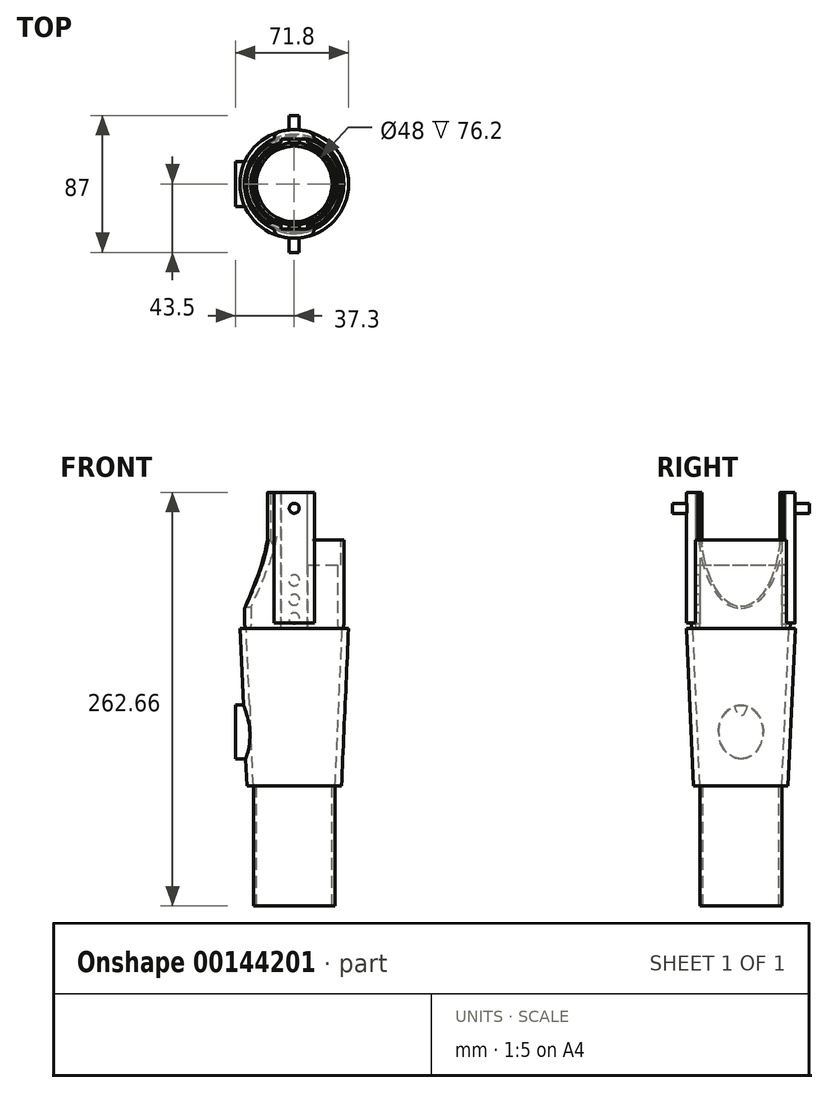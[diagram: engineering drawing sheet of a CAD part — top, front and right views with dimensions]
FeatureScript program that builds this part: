
annotation { "Feature Type Name" : "Feature", "Feature Type Description" : "" }
export const myFeature = defineFeature(function(context is Context, id is Id, definition is map)
    precondition{}
    {
        {
            var Q0;
            Q0=qCreatedBy(makeId("Top.planeOp"),FACE);
            var sketch = newSketch(context, id + "F0", { "sketchPlane" : qUnion([Q0])});
            skCircle(sketch, "E0", {"center": v(0, 0) * mm, "radius": 26 * mm});
            skSolve(sketch);
        }
        {
            var Q0;
            Q0=makeQuery(id+"F0.imprint","IMPRINT",FACE,{"disambiguationData":[TD([[makeQuery(id+"F0.imprint","IMPRINT",EDGE,{"derivedFrom":sQuery(id+"F0.wireOp",EDGE,"E0")}),1.0]])]});
            extrude(context, id + "F1", {"entities" : qUnion([Q0]), "depth" : 76.2 * mm});
        }
        {
            var Q0;
            Q0=makeQuery(id+"F1.opExtrude","CAP_FACE",FACE,{"disambiguationData":[OSD([sQuery(id+"F0.wireOp",EDGE,"E0")])],"isStart":false});
            cPlane(context, id + "F2", {"entities" : qUnion([Q0]), "cplaneType" : CPlaneType.OFFSET, "offset" : 0 * mm, "width" : 150 * mm, "height" : 150 * mm});
        }
        {
            var Q0;
            Q0=qCreatedBy(id+"F2.planeOp",FACE);
            var sketch = newSketch(context, id + "F3", { "sketchPlane" : qUnion([Q0])});
            skCircle(sketch, "E1.0", {"center": v(0, 0) * mm, "radius": 26 * mm});
            skSolve(sketch);
        }
        {
            var Q0;
            Q0=qCreatedBy(id+"F2.planeOp",FACE);
            cPlane(context, id + "F4", {"entities" : qUnion([Q0]), "cplaneType" : CPlaneType.OFFSET, "offset" : 100 * mm, "width" : 150 * mm, "height" : 150 * mm});
        }
        {
            var Q0;
            Q0=qCreatedBy(id+"F4.planeOp",FACE);
            var sketch = newSketch(context, id + "F5", { "sketchPlane" : qUnion([Q0])});
            skCircle(sketch, "E2", {"center": v(0, 0) * mm, "radius": 30.5 * mm});
            skSolve(sketch);
        }
        {
            var Q1;
            Q1=makeQuery(id+"F3.imprint","IMPRINT",FACE,{"disambiguationData":[TD([[makeQuery(id+"F3.imprint","IMPRINT",EDGE,{"derivedFrom":sQuery(id+"F3.wireOp",EDGE,"E1.0")}),1.0]])]});
            var Q2;
            Q2=makeQuery(id+"F5.imprint","IMPRINT",FACE,{"disambiguationData":[TD([[makeQuery(id+"F5.imprint","IMPRINT",EDGE,{"derivedFrom":sQuery(id+"F5.wireOp",EDGE,"E2")}),1.0]])]});
            loft(context, id + "F6", {"operationType" : NewBodyOperationType.ADD, "sheetProfilesArray" : [{ "sheetProfileEntities" : qUnion([Q1]) }, { "sheetProfileEntities" : qUnion([Q2]) }]});
        }
        {
            var Q0;
            Q0=qCreatedBy(id+"F2.planeOp",FACE);
            var sketch = newSketch(context, id + "F7", { "sketchPlane" : qUnion([Q0])});
            skCircle(sketch, "E3", {"center": v(0, 0) * mm, "radius": 24 * mm});
            skSolve(sketch);
        }
        {
            var Q0;
            Q0=qCreatedBy(id+"F4.planeOp",FACE);
            var sketch = newSketch(context, id + "F8", { "sketchPlane" : qUnion([Q0])});
            skCircle(sketch, "E4", {"center": v(0, 0) * mm, "radius": 28.5 * mm});
            skSolve(sketch);
        }
        {
            var Q1;
            Q1=makeQuery(id+"F8.imprint","IMPRINT",FACE,{"disambiguationData":[TD([[makeQuery(id+"F8.imprint","IMPRINT",EDGE,{"derivedFrom":sQuery(id+"F8.wireOp",EDGE,"E4")}),1.0]])]});
            var Q2;
            Q2=qSketchRegion(id+"F7",true);
            loft(context, id + "F9", {"operationType" : NewBodyOperationType.REMOVE, "sheetProfilesArray" : [{ "sheetProfileEntities" : qUnion([Q1]) }, { "sheetProfileEntities" : qUnion([Q2]) }]});
        }
        {
            var Q0;
            Q0=qCreatedBy(makeId("Top.planeOp"),FACE);
            var sketch = newSketch(context, id + "F10", { "sketchPlane" : qUnion([Q0])});
            skCircle(sketch, "E5", {"center": v(0, 0) * mm, "radius": 24 * mm});
            skSolve(sketch);
        }
        {
            var Q1;
            Q1=qSketchRegion(id+"F7",true);
            var Q2;
            Q2=qSketchRegion(id+"F10",true);
            loft(context, id + "F11", {"operationType" : NewBodyOperationType.REMOVE, "sheetProfilesArray" : [{ "sheetProfileEntities" : qUnion([Q1]) }, { "sheetProfileEntities" : qUnion([Q2]) }]});
        }
        {
            var Q0;
            Q0=qCreatedBy(id+"F4.planeOp",FACE);
            var sketch = newSketch(context, id + "F12", { "sketchPlane" : qUnion([Q0])});
            skCircle(sketch, "E6", {"center": v(0, 0) * mm, "radius": 31.5 * mm});
            skCircle(sketch, "E7.0", {"center": v(0, 0) * mm, "radius": 27.5 * mm});
            skSolve(sketch);
        }
        {
            var Q0;
            Q0=qSketchRegion(id+"F12",true);
            extrude(context, id + "F13", {"entities" : qUnion([Q0]), "operationType" : NewBodyOperationType.ADD, "depth" : 56.46 * mm});
        }
        {
            var Q0;
            Q0=makeQuery(id+"F13.opExtrude","CAP_EDGE",EDGE,{"disambiguationData":[OSD([sQuery(id+"F12.wireOp",EDGE,"E6")])],"isStart":true});
            fillet(context, id + "F14", {"entities" : qUnion([Q0]), "radius" : 5 * mm, "tangentPropagation" : true, "allowEdgeOverflow" : false});
        }
        {
            var Q0;
            Q0=makeQuery(id+"F13.opExtrude","CAP_FACE",FACE,{"disambiguationData":[OSD([sQuery(id+"F12.wireOp",EDGE,"E6"),sQuery(id+"F12.wireOp",EDGE,"E7.0")])],"isStart":false});
            cPlane(context, id + "F15", {"entities" : qUnion([Q0]), "cplaneType" : CPlaneType.OFFSET, "offset" : 0 * mm, "width" : 150 * mm, "height" : 150 * mm});
        }
        {
            var Q0;
            Q0=qCreatedBy(id+"F15.planeOp",FACE);
            var sketch = newSketch(context, id + "F16", { "sketchPlane" : qUnion([Q0])});
            skCircle(sketch, "E8.0", {"center": v(0, 0) * mm, "radius": 31.5 * mm, "construction": true});
            skCircle(sketch, "E9.0", {"center": v(0, 0) * mm, "radius": 27.5 * mm, "construction": true});
            skArc(sketch, "E10", {"start": v(8.5, -28.5) * mm, "mid": v(29.74, 0) * mm, "end": v(8.5, 28.5) * mm});
            skArc(sketch, "E11", {"start": v(8.5, -24.3) * mm, "mid": v(25.75, 0) * mm, "end": v(8.5, 24.3) * mm});
            skLineSegment(sketch, "E12", {"start": v(8.5, 28.5) * mm, "end": v(8.5, 24.3) * mm});
            skLineSegment(sketch, "E13.MirrorCS", {"start": v(8.5, -28.5) * mm, "end": v(8.5, -24.3) * mm});
            skPoint(sketch, "E14.orphan", {"position": v(0, 29.74) * mm});
            skPoint(sketch, "E15.orphan", {"position": v(0, -25.75) * mm});
            skSolve(sketch);
        }
        {
            var Q0;
            Q0=qSketchRegion(id+"F16",true);
            extrude(context, id + "F17", {"entities" : qUnion([Q0]), "operationType" : NewBodyOperationType.REMOVE, "oppositeDirection" : true, "depth" : 16 * mm});
        }
        {
            var Q0;
            Q0=qCreatedBy(id+"F15.planeOp",FACE);
            var sketch = newSketch(context, id + "F18", { "sketchPlane" : qUnion([Q0])});
            skLineSegment(sketch, "E16.bottom", {"start": v(-8.5, 28.5) * mm, "end": v(8.5, 28.5) * mm});
            skLineSegment(sketch, "E16.top", {"start": v(-8.5, 24) * mm, "end": v(8.5, 24) * mm});
            skLineSegment(sketch, "E16.left", {"start": v(-8.5, 28.5) * mm, "end": v(-8.5, 24) * mm});
            skLineSegment(sketch, "E16.right", {"start": v(8.5, 28.5) * mm, "end": v(8.5, 24) * mm});
            skLineSegment(sketch, "E17", {"start": v(0, 28.5) * mm, "end": v(0, 24) * mm, "construction": true});
            skLineSegment(sketch, "E18.0", {"start": v(8.5, -28.5) * mm, "end": v(8.5, -28.5) * mm});
            skLineSegment(sketch, "E19.MirrorCS", {"start": v(-8.5, -24) * mm, "end": v(8.5, -24) * mm});
            skLineSegment(sketch, "E20.MirrorCS", {"start": v(8.5, -28.5) * mm, "end": v(8.5, -24) * mm});
            skLineSegment(sketch, "E21.MirrorCS", {"start": v(-8.5, -28.5) * mm, "end": v(8.5, -28.5) * mm});
            skLineSegment(sketch, "E22.MirrorCS", {"start": v(-8.5, -28.5) * mm, "end": v(-8.5, -24) * mm});
            skSolve(sketch);
        }
        {
            var Q0;
            Q0=qSketchRegion(id+"F18",true);
            extrude(context, id + "F19", {"entities" : qUnion([Q0]), "operationType" : NewBodyOperationType.REMOVE, "oppositeDirection" : true, "depth" : 56.46 * mm});
        }
        {
            var Q0;
            {var subQ0=sQuery(id+"F12.wireOp",EDGE,"E7.0");Q0=makeQuery(id+"F19.boolean.opBoolean","SPLIT",EDGE,{"disambiguationData":[TD([makeQuery(id+"F19.opExtrude","SWEPT_FACE",FACE,{"disambiguationData":[OSD([sQuery(id+"F18.wireOp",EDGE,"E16.left")])]})])],"derivedFrom":makeQuery(id+"F13.opExtrude","CAP_EDGE",EDGE,{"disambiguationData":[OSD([subQ0])],"isStart":true})});}
            var Q1;
            {var subQ0=sQuery(id+"F12.wireOp",EDGE,"E7.0");Q1=makeQuery(id+"F19.boolean.opBoolean","SPLIT",EDGE,{"disambiguationData":[TD([makeQuery(id+"F19.opExtrude","SWEPT_FACE",FACE,{"disambiguationData":[OSD([sQuery(id+"F18.wireOp",EDGE,"E16.right")])]})])],"derivedFrom":makeQuery(id+"F13.opExtrude","CAP_EDGE",EDGE,{"disambiguationData":[OSD([subQ0])],"isStart":true})});}
            fillet(context, id + "F20", {"entities" : qUnion([Q0, Q1]), "radius" : 5 * mm, "tangentPropagation" : true, "allowEdgeOverflow" : false});
        }
        {
            var Q0;
            Q0=makeQuery(id+"F19.boolean.opBoolean","COPY",FACE,{"derivedFrom":makeQuery(id+"F19.opExtrude","SWEPT_FACE",FACE,{"disambiguationData":[OSD([sQuery(id+"F18.wireOp",EDGE,"E16.bottom")])]})});
            cPlane(context, id + "F21", {"entities" : qUnion([Q0]), "cplaneType" : CPlaneType.OFFSET, "offset" : 0 * mm, "width" : 150 * mm, "height" : 150 * mm});
        }
        {
            var Q0;
            Q0=qCreatedBy(id+"F21.planeOp",FACE);
            var sketch = newSketch(context, id + "F22", { "sketchPlane" : qUnion([Q0])});
            skLineSegment(sketch, "E23.0.0", {"start": v(8.5, 232.66) * mm, "end": v(-8.5, 232.66) * mm, "construction": true});
            skLineSegment(sketch, "E23.0.1", {"start": v(-8.5, 232.66) * mm, "end": v(-8.5, 176.2) * mm, "construction": true});
            skLineSegment(sketch, "E23.0.2", {"start": v(-8.5, 176.2) * mm, "end": v(0, 176.2) * mm, "construction": true});
            skLineSegment(sketch, "E23.0.3", {"start": v(0, 176.2) * mm, "end": v(8.5, 176.2) * mm, "construction": true});
            skLineSegment(sketch, "E23.0.4", {"start": v(8.5, 176.2) * mm, "end": v(8.5, 232.66) * mm, "construction": true});
            skLineSegment(sketch, "E24", {"start": v(0, 232.66) * mm, "end": v(0, 176.2) * mm, "construction": true});
            skCircle(sketch, "E25", {"center": v(0, 206.85) * mm, "radius": 3.45 * mm});
            skCircle(sketch, "E26", {"center": v(0, 194.54) * mm, "radius": 3.45 * mm});
            skCircle(sketch, "E27", {"center": v(0, 182.7) * mm, "radius": 3.45 * mm});
            skSolve(sketch);
        }
        {
            var Q0;
            Q0=qSketchRegion(id+"F22",true);
            extrude(context, id + "F23", {"entities" : qUnion([Q0]), "depth" : 2.5 * mm});
        }
        {
            var Q0;
            Q0=makeQuery(id+"F23.opExtrude","SWEPT_BODY",BODY,{"disambiguationData":[OSD([sQuery(id+"F22.wireOp",EDGE,"E25")])]});
            var Q1;
            Q1=makeQuery(id+"F23.opExtrude","SWEPT_BODY",BODY,{"disambiguationData":[OSD([sQuery(id+"F22.wireOp",EDGE,"E26")])]});
            var Q2;
            Q2=makeQuery(id+"F23.opExtrude","SWEPT_BODY",BODY,{"disambiguationData":[OSD([sQuery(id+"F22.wireOp",EDGE,"E27")])]});
            var Q3;
            Q3=qCreatedBy(makeId("Front.planeOp"),FACE);
            mirror(context, id + "F24", {"operationType" : NewBodyOperationType.ADD, "entities" : qUnion([Q0, Q1, Q2]), "mirrorPlane" : qUnion([Q3])});
        }
        {
            var Q0;
            Q0=qCreatedBy(id+"F15.planeOp",FACE);
            var sketch = newSketch(context, id + "F25", { "sketchPlane" : qUnion([Q0])});
            skCircle(sketch, "E28", {"center": v(0, 0) * mm, "radius": 34.44 * mm});
            skCircle(sketch, "E29.0", {"center": v(0, 0) * mm, "radius": 31.5 * mm});
            skLineSegment(sketch, "E30", {"start": v(12.77, 31.98) * mm, "end": v(12.77, 28.8) * mm});
            skLineSegment(sketch, "E31.MirrorCS", {"start": v(-12.77, 31.98) * mm, "end": v(-12.77, 28.8) * mm});
            skLineSegment(sketch, "E32.MirrorCS", {"start": v(12.77, -31.98) * mm, "end": v(12.77, -28.8) * mm});
            skLineSegment(sketch, "E33.MirrorCS", {"start": v(-12.77, -31.98) * mm, "end": v(-12.77, -28.8) * mm});
            skSolve(sketch);
        }
        {
            var Q0;
            {var subQ1=sQuery(id+"F25.wireOp",EDGE,"E30");Q0=makeQuery(id+"F25.imprint","IMPRINT",FACE,{"disambiguationData":[TD([[makeQuery(id+"F25.imprint","IMPRINT",EDGE,{"derivedFrom":subQ1}),-1.0]])]});}
            var Q1;
            {var subQ1=sQuery(id+"F25.wireOp",EDGE,"E32.MirrorCS");Q1=makeQuery(id+"F25.imprint","IMPRINT",FACE,{"disambiguationData":[TD([[makeQuery(id+"F25.imprint","IMPRINT",EDGE,{"derivedFrom":subQ1}),1.0]])]});}
            extrude(context, id + "F26", {"entities" : qUnion([Q0, Q1]), "operationType" : NewBodyOperationType.ADD, "depth" : 30 * mm, "hasSecondDirection" : true, "secondDirectionOppositeDirection" : true, "secondDirectionDepth" : 53 * mm});
        }
        {
            var Q0;
            Q0=makeQuery(id+"F13.opExtrude","CAP_FACE",FACE,{"disambiguationData":[OSD([sQuery(id+"F12.wireOp",EDGE,"E6"),sQuery(id+"F12.wireOp",EDGE,"E7.0")])],"isStart":false});
            var sketch = newSketch(context, id + "F27", { "sketchPlane" : qUnion([Q0])});
            skLineSegment(sketch, "E34", {"start": v(12.77, 28.8) * mm, "end": v(12.77, 26.86) * mm});
            skLineSegment(sketch, "E35", {"start": v(-12.77, 28.8) * mm, "end": v(-12.77, 24.35) * mm});
            skLineSegment(sketch, "E36.MirrorCS", {"start": v(12.77, -28.8) * mm, "end": v(12.77, -26.86) * mm});
            skLineSegment(sketch, "E37.MirrorCS", {"start": v(-12.77, -28.8) * mm, "end": v(-12.77, -24.35) * mm});
            skSolve(sketch);
        }
        {
            var Q0;
            {var subQ5=sQuery(id+"F27.wireOp",EDGE,"E34");Q0=makeQuery(id+"F27.imprint","IMPRINT",FACE,{"disambiguationData":[TD([[makeQuery(id+"F27.imprint","IMPRINT",EDGE,{"derivedFrom":subQ5}),-1.0]])]});}
            var Q1;
            {var subQ9=sQuery(id+"F27.wireOp",EDGE,"E36.MirrorCS");Q1=makeQuery(id+"F27.imprint","IMPRINT",FACE,{"disambiguationData":[TD([[makeQuery(id+"F27.imprint","IMPRINT",EDGE,{"derivedFrom":subQ9}),1.0]])]});}
            extrude(context, id + "F28", {"entities" : qUnion([Q0, Q1]), "operationType" : NewBodyOperationType.ADD, "depth" : 30 * mm, "hasSecondDirection" : true, "secondDirectionOppositeDirection" : true, "secondDirectionDepth" : 25 * mm});
        }
        {
            var Q0;
            Q0=makeQuery(id+"F26.opExtrude","SWEPT_EDGE",EDGE,{"disambiguationData":[OSD([sQuery(id+"F25.wireOp",EDGE,"E28"),sQuery(id+"F25.wireOp",EDGE,"E31.MirrorCS")])]});
            var Q1;
            Q1=makeQuery(id+"F26.opExtrude","SWEPT_EDGE",EDGE,{"disambiguationData":[OSD([sQuery(id+"F25.wireOp",EDGE,"E28"),sQuery(id+"F25.wireOp",EDGE,"E33.MirrorCS")])]});
            var Q2;
            Q2=makeQuery(id+"F26.opExtrude","SWEPT_EDGE",EDGE,{"disambiguationData":[OSD([sQuery(id+"F25.wireOp",EDGE,"E28"),sQuery(id+"F25.wireOp",EDGE,"E32.MirrorCS")])]});
            var Q3;
            Q3=makeQuery(id+"F26.opExtrude","SWEPT_EDGE",EDGE,{"disambiguationData":[OSD([sQuery(id+"F25.wireOp",EDGE,"E28"),sQuery(id+"F25.wireOp",EDGE,"E30")])]});
            fillet(context, id + "F29", {"entities" : qUnion([Q0, Q1, Q2, Q3]), "radius" : 5 * mm, "tangentPropagation" : true, "allowEdgeOverflow" : false});
        }
        {
            var Q0;
            Q0=makeQuery(id+"F28.opExtrude","SWEPT_EDGE",EDGE,{"disambiguationData":[OSD([sQuery(id+"F12.wireOp",EDGE,"E7.0"),sQuery(id+"F27.wireOp",EDGE,"E37.MirrorCS")])]});
            fillet(context, id + "F30", {"entities" : qUnion([Q0]), "radius" : 1 * mm, "tangentPropagation" : true, "allowEdgeOverflow" : false});
        }
        {
            var Q0;
            Q0=makeQuery(id+"F28.opExtrude","SWEPT_EDGE",EDGE,{"disambiguationData":[OSD([sQuery(id+"F12.wireOp",EDGE,"E7.0"),sQuery(id+"F27.wireOp",EDGE,"E35")])]});
            fillet(context, id + "F31", {"entities" : qUnion([Q0]), "radius" : 1 * mm, "tangentPropagation" : true, "allowEdgeOverflow" : false});
        }
        {
            var Q0;
            Q0=makeQuery(id+"F28.opExtrude","SWEPT_EDGE",EDGE,{"disambiguationData":[OSD([sQuery(id+"F16.wireOp",EDGE,"E10"),sQuery(id+"F27.wireOp",EDGE,"E36.MirrorCS")])]});
            fillet(context, id + "F32", {"entities" : qUnion([Q0]), "radius" : 1 * mm, "tangentPropagation" : true, "allowEdgeOverflow" : false});
        }
        {
            var Q0;
            Q0=makeQuery(id+"F28.opExtrude","SWEPT_EDGE",EDGE,{"disambiguationData":[OSD([sQuery(id+"F16.wireOp",EDGE,"E10"),sQuery(id+"F27.wireOp",EDGE,"E34")])]});
            fillet(context, id + "F33", {"entities" : qUnion([Q0]), "radius" : 1 * mm, "tangentPropagation" : true, "allowEdgeOverflow" : false});
        }
        {
            var Q0;
            {var subQ0=sQuery(id+"F18.wireOp",EDGE,"E16.bottom");Q0=makeQuery(id+"F28.boolean.opBoolean","MERGE",FACE,{"derivedFrom":[makeQuery(id+"F19.boolean.opBoolean","COPY",FACE,{"derivedFrom":makeQuery(id+"F19.opExtrude","SWEPT_FACE",FACE,{"disambiguationData":[OSD([subQ0])]})}),makeQuery(id+"F28.opExtrude","SWEPT_FACE",FACE,{"disambiguationData":[OSD([subQ0])]})]});}
            var sketch = newSketch(context, id + "F34", { "sketchPlane" : qUnion([Q0])});
            skLineSegment(sketch, "E38.0", {"start": v(-8.5, 262.66) * mm, "end": v(8.5, 262.66) * mm, "construction": true});
            skLineSegment(sketch, "E39", {"start": v(0, 262.66) * mm, "end": v(0, 242.66) * mm, "construction": true});
            skPoint(sketch, "E39.endSnap0", {"position": v(0, 262.66) * mm});
            skCircle(sketch, "E40", {"center": v(0, 252.66) * mm, "radius": 3.18 * mm});
            skSolve(sketch);
        }
        {
            var Q0;
            Q0=makeQuery(id+"F34.imprint","IMPRINT",FACE,{"disambiguationData":[TD([[makeQuery(id+"F34.imprint","IMPRINT",EDGE,{"derivedFrom":sQuery(id+"F34.wireOp",EDGE,"E40")}),1.0]])]});
            extrude(context, id + "F35", {"entities" : qUnion([Q0]), "oppositeDirection" : true, "depth" : 15 * mm});
        }
        {
            var Q0;
            Q0=makeQuery(id+"F35.opExtrude","SWEPT_BODY",BODY,{"disambiguationData":[OSD([sQuery(id+"F34.wireOp",EDGE,"E40")])]});
            var Q1;
            Q1=qCreatedBy(makeId("Front.planeOp"),FACE);
            mirror(context, id + "F36", {"operationType" : NewBodyOperationType.ADD, "entities" : qUnion([Q0]), "mirrorPlane" : qUnion([Q1])});
        }
        {
            var Q0;
            Q0=qCreatedBy(makeId("Right.planeOp"),FACE);
            cPlane(context, id + "F37", {"entities" : qUnion([Q0]), "cplaneType" : CPlaneType.OFFSET, "offset" : 55 * mm, "oppositeDirection" : true, "width" : 150 * mm, "height" : 150 * mm});
        }
        {
            var Q0;
            Q0=qCreatedBy(id+"F37.planeOp",FACE);
            var sketch = newSketch(context, id + "F38", { "sketchPlane" : qUnion([Q0])});
            skLineSegment(sketch, "E41", {"start": v(-31.5, 188.04) * mm, "end": v(-31.5, 188.5) * mm, "construction": true});
            skLineSegment(sketch, "E42", {"start": v(31.5, 188.5) * mm, "end": v(31.5, 188.04) * mm, "construction": true});
            skEllipse(sketch, "E43", {"center": v(0, 241.57) * mm, "majorRadius": 25.3 * mm, "minorRadius": 51.5 * mm, "majorAxis": v(-1, 0)});
            skSolve(sketch);
        }
        {
            var Q0;
            Q0=qSketchRegion(id+"F38",true);
            extrude(context, id + "F39", {"entities" : qUnion([Q0]), "operationType" : NewBodyOperationType.REMOVE, "depth" : 40 * mm});
        }
        {
            var Q0;
            Q0=makeQuery(id+"F39.boolean.opBoolean","INTERSECT",EDGE,{"derivedFrom":[makeQuery(id+"F13.opExtrude","SWEPT_FACE",FACE,{"disambiguationData":[OSD([sQuery(id+"F12.wireOp",EDGE,"E6")])]}),makeQuery(id+"F39.opExtrude","SWEPT_FACE",FACE,{"disambiguationData":[OSD([sQuery(id+"F38.wireOp",EDGE,"E43")])]})]});
            fillet(context, id + "F40", {"entities" : qUnion([Q0]), "radius" : 1 * mm, "tangentPropagation" : true, "allowEdgeOverflow" : false});
        }
        {
            var Q0;
            {var subQ0=sQuery(id+"F12.wireOp",EDGE,"E6");var subQ1=sQuery(id+"F12.wireOp",EDGE,"E7.0");var subQ6=sQuery(id+"F25.wireOp",EDGE,"E33.MirrorCS");var subQ7=makeQuery(id+"F26.opExtrude","SWEPT_FACE",FACE,{"disambiguationData":[OSD([subQ6])]});Q0=makeQuery(id+"F39.boolean.opBoolean","SPLIT",FACE,{"disambiguationData":[TD([subQ7])],"derivedFrom":makeQuery(id+"F28.boolean.opBoolean","SPLIT",FACE,{"disambiguationData":[TD([makeQuery(id+"F13.opExtrude","SWEPT_FACE",FACE,{"disambiguationData":[OSD([subQ1])]})])],"derivedFrom":makeQuery(id+"F13.opExtrude","CAP_FACE",FACE,{"disambiguationData":[OSD([subQ0,subQ1])],"isStart":false})})});}
            var Q1;
            {var subQ0=sQuery(id+"F12.wireOp",EDGE,"E6");var subQ1=sQuery(id+"F12.wireOp",EDGE,"E7.0");var subQ6=sQuery(id+"F25.wireOp",EDGE,"E31.MirrorCS");var subQ7=makeQuery(id+"F26.opExtrude","SWEPT_FACE",FACE,{"disambiguationData":[OSD([subQ6])]});Q1=makeQuery(id+"F39.boolean.opBoolean","SPLIT",FACE,{"disambiguationData":[TD([subQ7])],"derivedFrom":makeQuery(id+"F28.boolean.opBoolean","SPLIT",FACE,{"disambiguationData":[TD([makeQuery(id+"F13.opExtrude","SWEPT_FACE",FACE,{"disambiguationData":[OSD([subQ1])]})])],"derivedFrom":makeQuery(id+"F13.opExtrude","CAP_FACE",FACE,{"disambiguationData":[OSD([subQ0,subQ1])],"isStart":false})})});}
            var Q2;
            Q2=makeQuery(id+"F28.boolean.opBoolean","MERGE",FACE,{"derivedFrom":[makeQuery(id+"F26.opExtrude","CAP_FACE",FACE,{"disambiguationData":[OSD([sQuery(id+"F25.wireOp",EDGE,"E28"),sQuery(id+"F25.wireOp",EDGE,"E29.0"),sQuery(id+"F25.wireOp",EDGE,"E32.MirrorCS"),sQuery(id+"F25.wireOp",EDGE,"E33.MirrorCS")])],"isStart":false}),makeQuery(id+"F28.opExtrude","CAP_FACE",FACE,{"disambiguationData":[OSD([sQuery(id+"F12.wireOp",EDGE,"E6"),sQuery(id+"F12.wireOp",EDGE,"E7.0"),sQuery(id+"F16.wireOp",EDGE,"E10"),sQuery(id+"F18.wireOp",EDGE,"E20.MirrorCS"),sQuery(id+"F18.wireOp",EDGE,"E21.MirrorCS"),sQuery(id+"F18.wireOp",EDGE,"E22.MirrorCS"),sQuery(id+"F27.wireOp",EDGE,"E36.MirrorCS"),sQuery(id+"F27.wireOp",EDGE,"E37.MirrorCS")])],"isStart":false})]});
            extrude(context, id + "F41", {"entities" : qUnion([Q0, Q1]), "operationType" : NewBodyOperationType.ADD, "endBound" : BoundingType.UP_TO_SURFACE, "endBoundEntityFace" : qUnion([Q2]), "depth" : 25 * mm});
        }
        {
            var Q0;
            {var subQ0=sQuery(id+"F38.wireOp",EDGE,"E43");var subQ1=makeQuery(id+"F39.opExtrude","CAP_FACE",FACE,{"disambiguationData":[OSD([subQ0])],"isStart":false});var subQ2=sQuery(id+"F12.wireOp",EDGE,"E7.0");var subQ3=makeQuery(id+"F13.opExtrude","SWEPT_FACE",FACE,{"disambiguationData":[OSD([subQ2])]});var subQ5=sQuery(id+"F12.wireOp",EDGE,"E6");var subQ7=makeQuery(id+"F13.opExtrude","CAP_EDGE",EDGE,{"disambiguationData":[OSD([subQ2])],"isStart":false});var subQ8=sQuery(id+"F18.wireOp",EDGE,"E16.left");var subQ9=makeQuery(id+"F28.opExtrude","SWEPT_FACE",FACE,{"disambiguationData":[OSD([subQ2]),TDD([makeQuery(id+"F27.imprint","IMPRINT",EDGE,{"disambiguationData":[TD([[makeQuery(id+"F27.imprint","INTERSECT",VERTEX,{"derivedFrom":[makeQuery(id+"F19.boolean.opBoolean","COPY",EDGE,{"derivedFrom":makeQuery(id+"F19.opExtrude","CAP_EDGE",EDGE,{"disambiguationData":[OSD([subQ8])],"isStart":true})}),subQ7]}),1.0]])],"derivedFrom":subQ7})])]});var subQ10=sQuery(id+"F18.wireOp",EDGE,"E22.MirrorCS");var subQ11=makeQuery(id+"F28.opExtrude","SWEPT_FACE",FACE,{"disambiguationData":[OSD([subQ2]),TDD([makeQuery(id+"F27.imprint","IMPRINT",EDGE,{"disambiguationData":[TD([[makeQuery(id+"F27.imprint","INTERSECT",VERTEX,{"derivedFrom":[makeQuery(id+"F19.boolean.opBoolean","COPY",EDGE,{"derivedFrom":makeQuery(id+"F19.opExtrude","CAP_EDGE",EDGE,{"disambiguationData":[OSD([subQ10])],"isStart":true})}),subQ7]}),-1.0]])],"derivedFrom":subQ7})])]});var subQ12=makeQuery(id+"F13.opExtrude","CAP_FACE",FACE,{"disambiguationData":[OSD([subQ5,subQ2])],"isStart":false});var subQ13=makeQuery(id+"F28.boolean.opBoolean","MERGE",FACE,{"derivedFrom":[makeQuery(id+"F19.boolean.opBoolean","SPLIT",FACE,{"disambiguationData":[TD([makeQuery(id+"F19.opExtrude","SWEPT_FACE",FACE,{"disambiguationData":[OSD([subQ8])]})])],"derivedFrom":subQ3}),subQ9,subQ11]});Q0=makeQuery(id+"F41.boolean.opBoolean","MERGE",EDGE,{"derivedFrom":[makeQuery(id+"F39.boolean.opBoolean","INTERSECT",EDGE,{"disambiguationData":[OD(0.0)],"derivedFrom":[subQ13,subQ1]}),makeQuery(id+"F41.opExtrude","SWEPT_EDGE",EDGE,{"disambiguationData":[OSD([subQ5,subQ2,subQ0]),TDD([makeQuery(id+"F39.boolean.opBoolean","INTERSECT",VERTEX,{"disambiguationData":[OD(0.0)],"derivedFrom":[subQ13,makeQuery(id+"F28.boolean.opBoolean","SPLIT",FACE,{"disambiguationData":[TD([subQ3])],"derivedFrom":subQ12}),subQ1]})])]})]});}
            var Q1;
            {var subQ0=sQuery(id+"F38.wireOp",EDGE,"E43");var subQ1=makeQuery(id+"F39.opExtrude","CAP_FACE",FACE,{"disambiguationData":[OSD([subQ0])],"isStart":false});var subQ2=sQuery(id+"F12.wireOp",EDGE,"E7.0");var subQ3=makeQuery(id+"F13.opExtrude","SWEPT_FACE",FACE,{"disambiguationData":[OSD([subQ2])]});var subQ5=sQuery(id+"F12.wireOp",EDGE,"E6");var subQ7=makeQuery(id+"F13.opExtrude","CAP_EDGE",EDGE,{"disambiguationData":[OSD([subQ2])],"isStart":false});var subQ8=sQuery(id+"F18.wireOp",EDGE,"E16.left");var subQ9=makeQuery(id+"F28.opExtrude","SWEPT_FACE",FACE,{"disambiguationData":[OSD([subQ2]),TDD([makeQuery(id+"F27.imprint","IMPRINT",EDGE,{"disambiguationData":[TD([[makeQuery(id+"F27.imprint","INTERSECT",VERTEX,{"derivedFrom":[makeQuery(id+"F19.boolean.opBoolean","COPY",EDGE,{"derivedFrom":makeQuery(id+"F19.opExtrude","CAP_EDGE",EDGE,{"disambiguationData":[OSD([subQ8])],"isStart":true})}),subQ7]}),1.0]])],"derivedFrom":subQ7})])]});var subQ10=sQuery(id+"F18.wireOp",EDGE,"E22.MirrorCS");var subQ11=makeQuery(id+"F28.opExtrude","SWEPT_FACE",FACE,{"disambiguationData":[OSD([subQ2]),TDD([makeQuery(id+"F27.imprint","IMPRINT",EDGE,{"disambiguationData":[TD([[makeQuery(id+"F27.imprint","INTERSECT",VERTEX,{"derivedFrom":[makeQuery(id+"F19.boolean.opBoolean","COPY",EDGE,{"derivedFrom":makeQuery(id+"F19.opExtrude","CAP_EDGE",EDGE,{"disambiguationData":[OSD([subQ10])],"isStart":true})}),subQ7]}),-1.0]])],"derivedFrom":subQ7})])]});var subQ12=makeQuery(id+"F13.opExtrude","CAP_FACE",FACE,{"disambiguationData":[OSD([subQ5,subQ2])],"isStart":false});var subQ13=makeQuery(id+"F28.boolean.opBoolean","MERGE",FACE,{"derivedFrom":[makeQuery(id+"F19.boolean.opBoolean","SPLIT",FACE,{"disambiguationData":[TD([makeQuery(id+"F19.opExtrude","SWEPT_FACE",FACE,{"disambiguationData":[OSD([subQ8])]})])],"derivedFrom":subQ3}),subQ9,subQ11]});Q1=makeQuery(id+"F41.boolean.opBoolean","MERGE",EDGE,{"derivedFrom":[makeQuery(id+"F39.boolean.opBoolean","INTERSECT",EDGE,{"disambiguationData":[OD(1.0)],"derivedFrom":[subQ13,subQ1]}),makeQuery(id+"F41.opExtrude","SWEPT_EDGE",EDGE,{"disambiguationData":[OSD([subQ5,subQ2,subQ0]),TDD([makeQuery(id+"F39.boolean.opBoolean","INTERSECT",VERTEX,{"disambiguationData":[OD(1.0)],"derivedFrom":[subQ13,makeQuery(id+"F28.boolean.opBoolean","SPLIT",FACE,{"disambiguationData":[TD([subQ3])],"derivedFrom":subQ12}),subQ1]})])]})]});}
            fillet(context, id + "F42", {"entities" : qUnion([Q0, Q1]), "radius" : 5 * mm, "tangentPropagation" : true, "allowEdgeOverflow" : false});
        }
        {
            var Q0;
            Q0=qCreatedBy(makeId("Top.planeOp"),FACE);
            cPlane(context, id + "F43", {"entities" : qUnion([Q0]), "cplaneType" : CPlaneType.OFFSET, "offset" : 90 * mm, "width" : 150 * mm, "height" : 150 * mm});
        }
        {
            var Q0;
            Q0=qCreatedBy(id+"F2.planeOp",FACE);
            var sketch = newSketch(context, id + "F44", { "sketchPlane" : qUnion([Q0])});
            skCircle(sketch, "E44", {"center": v(0, 0) * mm, "radius": 30 * mm});
            skSolve(sketch);
        }
        {
            var Q0;
            Q0=qCreatedBy(id+"F4.planeOp",FACE);
            var sketch = newSketch(context, id + "F45", { "sketchPlane" : qUnion([Q0])});
            skCircle(sketch, "E45", {"center": v(0, 0) * mm, "radius": 34.5 * mm});
            skSolve(sketch);
        }
        {
            var Q1;
            Q1=makeQuery(id+"F44.imprint","IMPRINT",FACE,{"disambiguationData":[TD([[makeQuery(id+"F44.imprint","IMPRINT",EDGE,{"derivedFrom":sQuery(id+"F44.wireOp",EDGE,"E44")}),1.0]])]});
            var Q2;
            Q2=makeQuery(id+"F45.imprint","IMPRINT",FACE,{"disambiguationData":[TD([[makeQuery(id+"F45.imprint","IMPRINT",EDGE,{"derivedFrom":sQuery(id+"F45.wireOp",EDGE,"E45")}),1.0]])]});
            loft(context, id + "F46", {"sheetProfilesArray" : [{ "sheetProfileEntities" : qUnion([Q1]) }, { "sheetProfileEntities" : qUnion([Q2]) }]});
        }
        {
            var Q0;
            Q0=qCreatedBy(id+"F4.planeOp",FACE);
            var sketch = newSketch(context, id + "F47", { "sketchPlane" : qUnion([Q0])});
            skCircle(sketch, "E46.0", {"center": v(0, 0) * mm, "radius": 30.5 * mm});
            skSolve(sketch);
        }
        {
            var Q0;
            Q0=qCreatedBy(id+"F2.planeOp",FACE);
            var sketch = newSketch(context, id + "F48", { "sketchPlane" : qUnion([Q0])});
            skCircle(sketch, "E47.0", {"center": v(0, 0) * mm, "radius": 26 * mm});
            skSolve(sketch);
        }
        {
            var Q0;
            Q0 = qSketchRegion(id + "F48", true);
            var Q1;
            Q1 = qSketchRegion(id + "F47", true);
            loft(context, id + "F49", {"operationType" : NewBodyOperationType.REMOVE, "sheetProfilesArray" : [{ "sheetProfileEntities" : qUnion([Q0]) }, { "sheetProfileEntities" : qUnion([Q1]) }]});
        }
        {
            var Q0;
            Q0=qCreatedBy(makeId("Right.planeOp"),FACE);
            var sketch = newSketch(context, id + "F50", { "sketchPlane" : qUnion([Q0])});
            skEllipse(sketch, "E48", {"center": v(0, 110.6) * mm, "majorRadius": 14.23 * mm, "minorRadius": 17.1 * mm, "majorAxis": v(-1, 0)});
            skSolve(sketch);
        }
        {
            var Q0;
            Q0=qCreatedBy(makeId("Right.planeOp"),FACE);
            cPlane(context, id + "F51", {"entities" : qUnion([Q0]), "cplaneType" : CPlaneType.OFFSET, "offset" : 28 * mm, "oppositeDirection" : true, "width" : 150 * mm, "height" : 150 * mm});
        }
        {
            var Q0;
            Q0=qCreatedBy(id+"F51.planeOp",FACE);
            var sketch = newSketch(context, id + "F52", { "sketchPlane" : qUnion([Q0])});
            skEllipse(sketch, "E49.0", {"center": v(0, 110.6) * mm, "majorRadius": 17.1 * mm, "minorRadius": 14.23 * mm, "majorAxis": v(0, -1)});
            skSolve(sketch);
        }
        {
            var Q0;
            Q0 = qSketchRegion(id + "F52", true);
            extrude(context, id + "F53", {"entities" : qUnion([Q0]), "operationType" : NewBodyOperationType.ADD, "oppositeDirection" : true, "depth" : 9.3 * mm});
        }
    });
